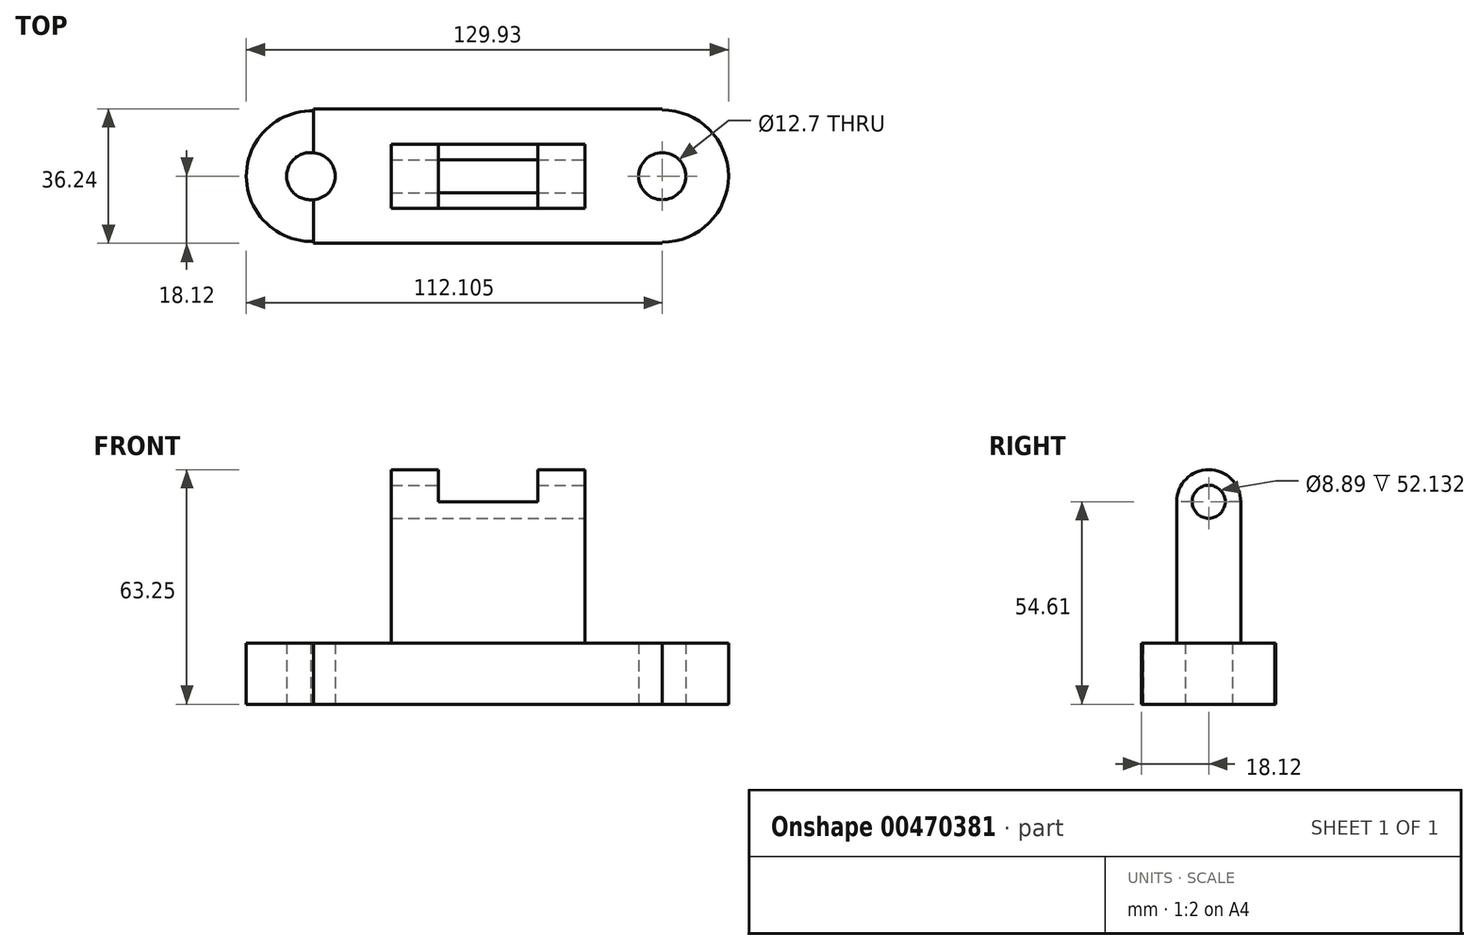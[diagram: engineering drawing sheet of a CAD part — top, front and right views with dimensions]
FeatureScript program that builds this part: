
annotation { "Feature Type Name" : "Feature", "Feature Type Description" : "" }
export const myFeature = defineFeature(function(context is Context, id is Id, definition is map)
    precondition{}
    {
        {
            var Q0;
            Q0=qCreatedBy(makeId("Top.planeOp"),FACE);
            var sketch = newSketch(context, id + "F0", { "sketchPlane" : qUnion([Q0])});
            skLineSegment(sketch, "E0.bottom", {"start": v(-46.97, 18.12) * mm, "end": v(46.97, 18.12) * mm});
            skLineSegment(sketch, "E0.top", {"start": v(-46.97, -18.12) * mm, "end": v(46.97, -18.12) * mm});
            skLineSegment(sketch, "E0.left", {"start": v(-46.97, 18.12) * mm, "end": v(-46.97, -18.12) * mm});
            skLineSegment(sketch, "E0.right", {"start": v(46.97, 18.12) * mm, "end": v(46.97, -18.12) * mm});
            skPoint(sketch, "E0.middle", {"position": v(0, 0) * mm});
            skSolve(sketch);
        }
        {
            var Q0;
            Q0=makeQuery(id+"F0.imprint","IMPRINT",FACE,{"disambiguationData":[TD([[makeQuery(id+"F0.imprint","IMPRINT",EDGE,{"derivedFrom":sQuery(id+"F0.wireOp",EDGE,"E0.bottom")}),-1.0]])]});
            var sketch = newSketch(context, id + "F1", { "sketchPlane" : qUnion([Q0])});
            skCircle(sketch, "E1", {"center": v(46.97, 0) * mm, "radius": 17.83 * mm});
            skSolve(sketch);
        }
        {
            var Q0;
            Q0=makeQuery(id+"F0.imprint","IMPRINT",FACE,{"disambiguationData":[TD([[makeQuery(id+"F0.imprint","IMPRINT",EDGE,{"derivedFrom":sQuery(id+"F0.wireOp",EDGE,"E0.bottom")}),-1.0]])]});
            var sketch = newSketch(context, id + "F2", { "sketchPlane" : qUnion([Q0])});
            skCircle(sketch, "E2", {"center": v(-47.53, 0) * mm, "radius": 17.6 * mm});
            skSolve(sketch);
        }
        {
            var Q0;
            {var subQ0=sQuery(id+"F2.wireOp",EDGE,"E2");var subQ1=makeQuery(id+"F0.imprint","IMPRINT",EDGE,{"derivedFrom":sQuery(id+"F0.wireOp",EDGE,"E0.left")});var subQ2=makeQuery(id+"F2.imprint","INTERSECT",VERTEX,{"disambiguationData":[OD(0.0)],"derivedFrom":[subQ1,subQ0]});Q0=makeQuery(id+"F2.imprint","IMPRINT",FACE,{"disambiguationData":[TD([[makeQuery(id+"F2.imprint","IMPRINT",EDGE,{"disambiguationData":[TD([[subQ2,-1.0]])],"derivedFrom":subQ0}),1.0]])]});}
            var sketch = newSketch(context, id + "F3", { "sketchPlane" : qUnion([Q0])});
            skPoint(sketch, "E3", {"position": v(6.41, -48.02) * mm});
            skPoint(sketch, "E4", {"position": v(-47.93, 0) * mm});
            skPoint(sketch, "E5", {"position": v(46.74, 0) * mm});
            skSolve(sketch);
        }
        {
            var Q0;
            {var subQ1=makeQuery(id+"F0.imprint","IMPRINT",EDGE,{"derivedFrom":sQuery(id+"F0.wireOp",EDGE,"E0.bottom")});Q0=makeQuery(id+"F1.imprint","IMPRINT",FACE,{"disambiguationData":[TD([[makeQuery(id+"F1.imprint","IMPRINT",EDGE,{"derivedFrom":subQ1}),-1.0]])]});}
            var Q1;
            {var subQ0=sQuery(id+"F2.wireOp",EDGE,"E2");var subQ1=makeQuery(id+"F0.imprint","IMPRINT",EDGE,{"derivedFrom":sQuery(id+"F0.wireOp",EDGE,"E0.left")});var subQ2=makeQuery(id+"F2.imprint","INTERSECT",VERTEX,{"disambiguationData":[OD(0.0)],"derivedFrom":[subQ1,subQ0]});Q1=makeQuery(id+"F2.imprint","IMPRINT",FACE,{"disambiguationData":[TD([[makeQuery(id+"F2.imprint","IMPRINT",EDGE,{"disambiguationData":[TD([[subQ2,-1.0]])],"derivedFrom":subQ0}),1.0]])]});}
            extrude(context, id + "F4", {"entities" : qUnion([Q0, Q1]), "depth" : 16.5 * mm});
        }
        {
            var Q0;
            Q0=sQuery(id+"F1.wireOp",EDGE,"E1");
            extrude(context, id + "F5", {"bodyType" : ToolBodyType.SURFACE, "surfaceEntities" : qUnion([Q0]), "depth" : 16.5 * mm});
        }
        {
            var Q0;
            {var subQ0=sQuery(id+"F1.wireOp",EDGE,"E1");var subQ1=makeQuery(id+"F0.imprint","IMPRINT",EDGE,{"derivedFrom":sQuery(id+"F0.wireOp",EDGE,"E0.right")});var subQ2=makeQuery(id+"F1.imprint","INTERSECT",VERTEX,{"disambiguationData":[OD(0.0)],"derivedFrom":[subQ1,subQ0]});Q0=makeQuery(id+"F1.imprint","IMPRINT",FACE,{"disambiguationData":[TD([[makeQuery(id+"F1.imprint","IMPRINT",EDGE,{"disambiguationData":[TD([[subQ2,1.0]])],"derivedFrom":subQ0}),1.0]])]});}
            var Q1;
            {var subQ0=sQuery(id+"F1.wireOp",EDGE,"E1");var subQ1=makeQuery(id+"F0.imprint","IMPRINT",EDGE,{"derivedFrom":sQuery(id+"F0.wireOp",EDGE,"E0.right")});var subQ2=makeQuery(id+"F1.imprint","INTERSECT",VERTEX,{"disambiguationData":[OD(0.0)],"derivedFrom":[subQ1,subQ0]});Q1=makeQuery(id+"F1.imprint","IMPRINT",FACE,{"disambiguationData":[TD([[makeQuery(id+"F1.imprint","IMPRINT",EDGE,{"disambiguationData":[TD([[subQ2,-1.0]])],"derivedFrom":subQ0}),1.0]])]});}
            extrude(context, id + "F6", {"entities" : qUnion([Q0, Q1]), "operationType" : NewBodyOperationType.ADD, "depth" : 16.5 * mm});
        }
        {
            var Q0;
            Q0=sQuery(id+"F3.wireOp",VERTEX,"E4");
            var Q1;
            Q1=makeQuery(id+"F4.opExtrude","SWEPT_BODY",BODY,{"disambiguationData":[OSD([sQuery(id+"F0.wireOp",EDGE,"E0.left"),sQuery(id+"F2.wireOp",EDGE,"E2")])]});
            hole(context, id + "F7", {"style" : HoleStyle.SIMPLE, "endStyle" : HoleEndStyle.THROUGH, "oppositeDirection" : true, "holeDiameter" : 12.7 * mm, "isTappedThrough" : true, "tappedDepth" : 12.7 * mm, "tapClearance" : 3, "locations" : qUnion([Q0]), "scope" : qUnion([Q1])});
        }
        {
            var Q0;
            Q0=sQuery(id+"F1.wireOp",VERTEX,"E1.center");
            var Q1;
            Q1=makeQuery(id+"F4.opExtrude","SWEPT_BODY",BODY,{"disambiguationData":[OSD([sQuery(id+"F0.wireOp",EDGE,"E0.bottom"),sQuery(id+"F0.wireOp",EDGE,"E0.top"),sQuery(id+"F0.wireOp",EDGE,"E0.left"),sQuery(id+"F0.wireOp",EDGE,"E0.right"),sQuery(id+"F1.wireOp",EDGE,"E1")])]});
            hole(context, id + "F8", {"style" : HoleStyle.SIMPLE, "endStyle" : HoleEndStyle.THROUGH, "oppositeDirection" : true, "holeDiameter" : 12.7 * mm, "isTappedThrough" : true, "tappedDepth" : 12.7 * mm, "tapClearance" : 3, "locations" : qUnion([Q0]), "scope" : qUnion([Q1])});
        }
        {
            var Q0;
            Q0=sQuery(id+"F2.wireOp",VERTEX,"E2.center");
            var Q1;
            Q1=makeQuery(id+"F4.opExtrude","SWEPT_BODY",BODY,{"disambiguationData":[OSD([sQuery(id+"F0.wireOp",EDGE,"E0.bottom"),sQuery(id+"F0.wireOp",EDGE,"E0.top"),sQuery(id+"F0.wireOp",EDGE,"E0.left"),sQuery(id+"F0.wireOp",EDGE,"E0.right"),sQuery(id+"F1.wireOp",EDGE,"E1")])]});
            var Q2;
            Q2=makeQuery(id+"F4.opExtrude","SWEPT_BODY",BODY,{"disambiguationData":[OSD([sQuery(id+"F0.wireOp",EDGE,"E0.left"),sQuery(id+"F2.wireOp",EDGE,"E2")])]});
            hole(context, id + "F9", {"style" : HoleStyle.SIMPLE, "endStyle" : HoleEndStyle.THROUGH, "oppositeDirection" : true, "holeDiameter" : 12.7 * mm, "isTappedThrough" : true, "tappedDepth" : 12.7 * mm, "tapClearance" : 3, "locations" : qUnion([Q0]), "scope" : qUnion([Q1, Q2])});
        }
        {
            var Q0;
            {var subQ0=sQuery(id+"F1.wireOp",EDGE,"E1");Q0=makeQuery(id+"F6.boolean.opBoolean","MERGE",FACE,{"derivedFrom":[makeQuery(id+"F4.opExtrude","CAP_FACE",FACE,{"disambiguationData":[OSD([sQuery(id+"F0.wireOp",EDGE,"E0.bottom"),sQuery(id+"F0.wireOp",EDGE,"E0.top"),sQuery(id+"F0.wireOp",EDGE,"E0.left"),sQuery(id+"F0.wireOp",EDGE,"E0.right"),subQ0])],"isStart":false}),makeQuery(id+"F6.opExtrude","CAP_FACE",FACE,{"disambiguationData":[OSD([subQ0])],"isStart":false})]});}
            var sketch = newSketch(context, id + "F10", { "sketchPlane" : qUnion([Q0])});
            skLineSegment(sketch, "E6.bottom", {"start": v(-26.07, 8.64) * mm, "end": v(26.07, 8.64) * mm});
            skLineSegment(sketch, "E6.top", {"start": v(-26.07, -8.64) * mm, "end": v(26.07, -8.64) * mm});
            skLineSegment(sketch, "E6.left", {"start": v(-26.07, 8.64) * mm, "end": v(-26.07, -8.64) * mm});
            skLineSegment(sketch, "E6.right", {"start": v(26.07, 8.64) * mm, "end": v(26.07, -8.64) * mm});
            skPoint(sketch, "E6.middle", {"position": v(0, 0) * mm});
            skSolve(sketch);
        }
        {
            var Q0;
            Q0=makeQuery(id+"F10.imprint","IMPRINT",FACE,{"disambiguationData":[TD([[makeQuery(id+"F10.imprint","IMPRINT",EDGE,{"derivedFrom":sQuery(id+"F10.wireOp",EDGE,"E6.bottom")}),-1.0]])]});
            extrude(context, id + "F11", {"entities" : qUnion([Q0]), "operationType" : NewBodyOperationType.ADD, "depth" : 38.1 * mm});
        }
        {
            var Q0;
            Q0=makeQuery(id+"F11.opExtrude","SWEPT_FACE",FACE,{"disambiguationData":[OSD([sQuery(id+"F10.wireOp",EDGE,"E6.left")])]});
            var sketch = newSketch(context, id + "F12", { "sketchPlane" : qUnion([Q0])});
            skArc(sketch, "E7", {"start": v(8.64, 54.61) * mm, "mid": v(0, 63.25) * mm, "end": v(-8.64, 54.61) * mm});
            skSolve(sketch);
        }
        {
            var Q0;
            Q0=makeQuery(id+"F12.imprint","IMPRINT",FACE,{"disambiguationData":[TD([[makeQuery(id+"F12.imprint","IMPRINT",EDGE,{"derivedFrom":sQuery(id+"F12.wireOp",EDGE,"E7")}),1.0]])]});
            extrude(context, id + "F13", {"entities" : qUnion([Q0]), "operationType" : NewBodyOperationType.ADD, "oppositeDirection" : true, "depth" : 12.7 * mm});
        }
        {
            var Q0;
            Q0=makeQuery(id+"F11.opExtrude","SWEPT_FACE",FACE,{"disambiguationData":[OSD([sQuery(id+"F10.wireOp",EDGE,"E6.right")])]});
            var sketch = newSketch(context, id + "F14", { "sketchPlane" : qUnion([Q0])});
            skArc(sketch, "E8", {"start": v(8.64, 54.61) * mm, "mid": v(0, 63.25) * mm, "end": v(-8.64, 54.61) * mm});
            skSolve(sketch);
        }
        {
            var Q0;
            Q0=makeQuery(id+"F14.imprint","IMPRINT",FACE,{"disambiguationData":[TD([[makeQuery(id+"F14.imprint","IMPRINT",EDGE,{"derivedFrom":sQuery(id+"F14.wireOp",EDGE,"E8")}),1.0]])]});
            extrude(context, id + "F15", {"entities" : qUnion([Q0]), "operationType" : NewBodyOperationType.ADD, "oppositeDirection" : true, "depth" : 12.7 * mm});
        }
        {
            var Q0;
            {var subQ0=sQuery(id+"F10.wireOp",EDGE,"E6.right");Q0=makeQuery(id+"F15.boolean.opBoolean","MERGE",FACE,{"derivedFrom":[makeQuery(id+"F11.opExtrude","SWEPT_FACE",FACE,{"disambiguationData":[OSD([subQ0])]}),makeQuery(id+"F15.opExtrude","CAP_FACE",FACE,{"disambiguationData":[OSD([subQ0,sQuery(id+"F14.wireOp",EDGE,"E8")])],"isStart":true})]});}
            var sketch = newSketch(context, id + "F16", { "sketchPlane" : qUnion([Q0])});
            skPoint(sketch, "E9", {"position": v(0, 54.61) * mm});
            skSolve(sketch);
        }
        {
            var Q0;
            Q0=sQuery(id+"F16.wireOp",VERTEX,"E9");
            var Q1;
            Q1=makeQuery(id+"F4.opExtrude","SWEPT_BODY",BODY,{"disambiguationData":[OSD([sQuery(id+"F0.wireOp",EDGE,"E0.bottom"),sQuery(id+"F0.wireOp",EDGE,"E0.top"),sQuery(id+"F0.wireOp",EDGE,"E0.left"),sQuery(id+"F0.wireOp",EDGE,"E0.right"),sQuery(id+"F1.wireOp",EDGE,"E1")])]});
            hole(context, id + "F17", {"style" : HoleStyle.SIMPLE, "endStyle" : HoleEndStyle.THROUGH, "holeDiameter" : 8.9 * mm, "isTappedThrough" : true, "tappedDepth" : 12.7 * mm, "tapClearance" : 3, "locations" : qUnion([Q0]), "scope" : qUnion([Q1])});
        }
    });
